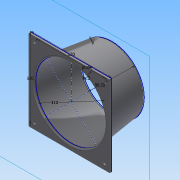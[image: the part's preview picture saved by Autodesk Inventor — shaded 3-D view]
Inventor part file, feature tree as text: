
AUTODESK INVENTOR PART (.ipt)
format: ipt  version: 2014 SP2 (Build 180246200, 246)  size: 167,424 bytes
history: native  units: mm
features: extrude x3, sketch x2, loft x2, fillet x2, hole x1, pattern_circular x1, plane x1, shell x1
ambient origin geometry x8: Origin, YZ Plane, XZ Plane, XY Plane, X Axis, Y Axis, Z Axis, Center Point
bodies: Solid1 (feature_tree)
feature tree (13):
  sketch  "Sketch1"  dims[d0=120.0mm d1=120.0mm]
  extrude  "Extrusion1"  Depth=120.0mm
  hole  "Hole1"  [1 undecoded]
  pattern_circular  "Circular Pattern1"  [2 undecoded]
  plane  "Work Plane1"
  sketch  "Sketch3"  dims[d2=112.0mm d4=104.0mm d5=3.0mm d6=0.0mm d7=4.4mm d8=6.0mm d9=4.0mm d10=2.0mm d11=90.0deg d12=8.0mm d13=20.594885mm d14=40.0mm d15=360.0deg d17=20.0mm d18=-3.490659mm d19=3.0mm d20=60.0mm d21=96.52mm d22=0.0mm d23=90.0deg d24=0.0mm d25=90.0deg d27=20.0mm d28=0.0mm d29=3.0mm d30=0.0mm d31=90.0deg d32=0.0mm d33=90.0deg d35=2.0mm d36=1.5mm]
  loft  "Loft1"
  loft  "Loft2"
  fillet  "Fillet1"  Radius=3.0mm
  fillet  "Fillet2"  Radius=60.0mm
  extrude  "Extrusion2"  Depth=1.5mm
  shell  "Shell1"  Thickness=0.0mm
  extrude  "Extrusion3"  TaperAngle=0.0deg  [1 undecoded]
note: 4 required parameter values undecoded (feature->parameter linkage not recoverable at this tier; creation-order binding heuristic only, values carry confidence <= 0.55)
